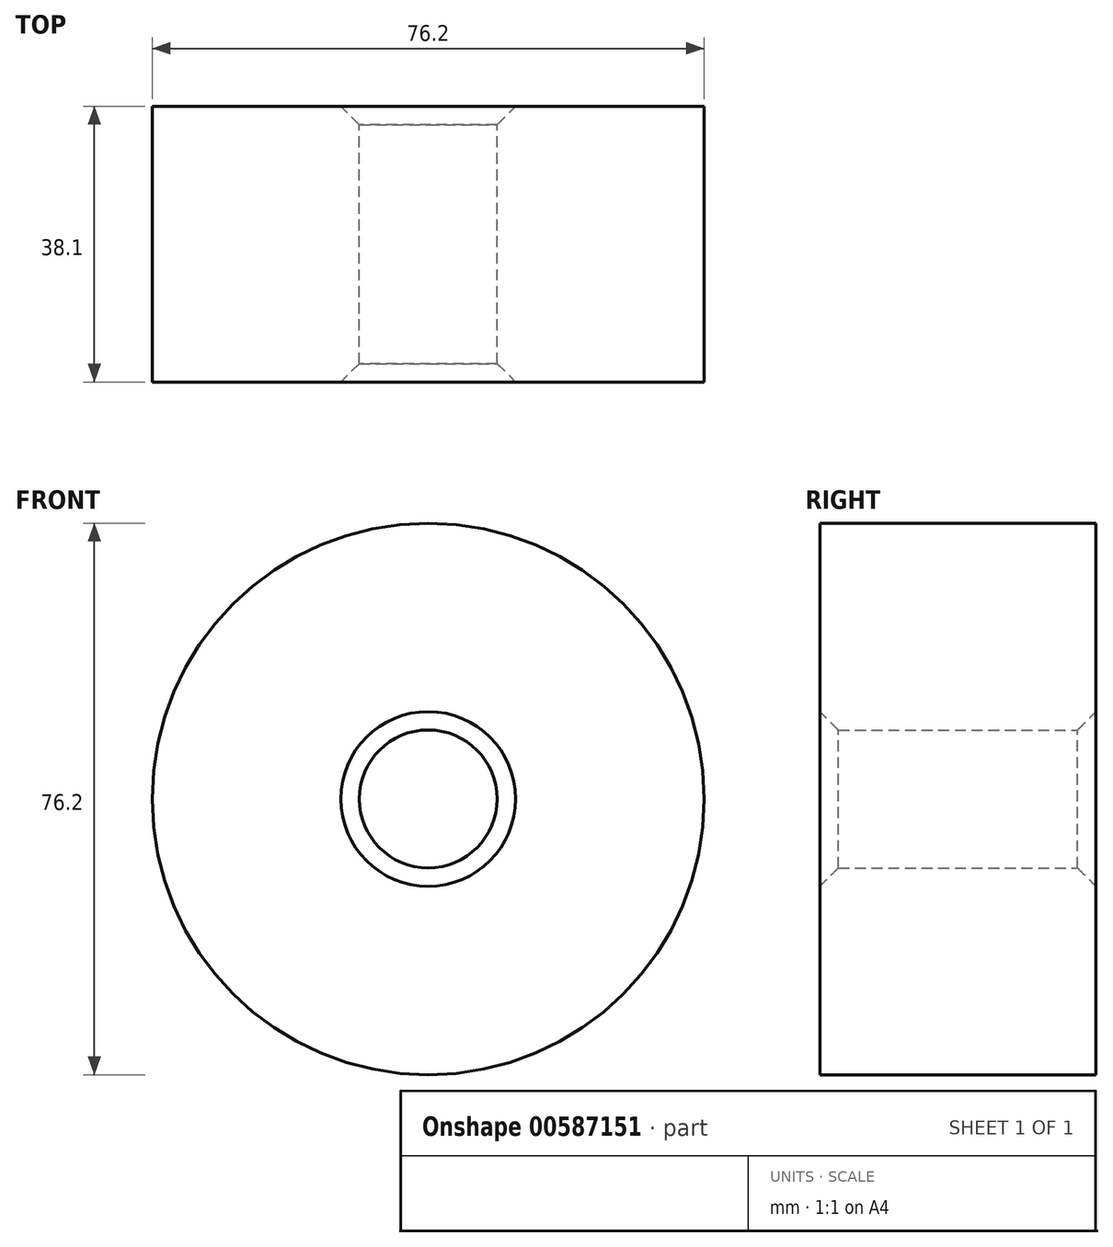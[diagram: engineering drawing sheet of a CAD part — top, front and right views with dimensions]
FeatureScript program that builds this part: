
annotation { "Feature Type Name" : "Feature", "Feature Type Description" : "" }
export const myFeature = defineFeature(function(context is Context, id is Id, definition is map)
    precondition{}
    {
        {
            var Q0;
            Q0=qCreatedBy(makeId("Front.planeOp"),FACE);
            var sketch = newSketch(context, id + "F0", { "sketchPlane" : qUnion([Q0])});
            skCircle(sketch, "E0", {"center": v(-51.5, 0) * mm, "radius": 38.1 * mm});
            skCircle(sketch, "E1", {"center": v(75.5, 0) * mm, "radius": 25.4 * mm});
            skCircle(sketch, "E2", {"center": v(-51.5, 0) * mm, "radius": 9.53 * mm});
            skCircle(sketch, "E3", {"center": v(75.5, 0) * mm, "radius": 9.53 * mm});
            skSolve(sketch);
        }
        {
            var Q0;
            Q0 = qSketchRegion(id + "F0", true);
            var sketch = newSketch(context, id + "F1", { "sketchPlane" : qUnion([Q0])});
            skLineSegment(sketch, "E4", {"start": v(-50.16, 38.16) * mm, "end": v(78.48, 25.23) * mm});
            skLineSegment(sketch, "E5", {"start": v(-53.26, -38.47) * mm, "end": v(78.52, -25.22) * mm});
            skSolve(sketch);
        }
        {
            var Q0;
            Q0=makeQuery(id+"F1.imprint","IMPRINT",FACE,{"disambiguationData":[TD([[makeQuery(id+"F1.imprint","IMPRINT",EDGE,{"derivedFrom":makeQuery(id+"F0.imprint","IMPRINT",EDGE,{"derivedFrom":sQuery(id+"F0.wireOp",EDGE,"E2")})}),-1.0]])]});
            var Q1;
            {var subQ0=sQuery(id+"F1.wireOp",EDGE,"E4");var subQ1=makeQuery(id+"F0.imprint","IMPRINT",EDGE,{"derivedFrom":sQuery(id+"F0.wireOp",EDGE,"E0")});var subQ2=makeQuery(id+"F1.imprint","INTERSECT",VERTEX,{"derivedFrom":[subQ1,subQ0]});Q1=makeQuery(id+"F1.imprint","IMPRINT",FACE,{"disambiguationData":[TD([[makeQuery(id+"F1.imprint","IMPRINT",EDGE,{"disambiguationData":[TD([[subQ2,-1.0]])],"derivedFrom":subQ0}),-1.0]])]});}
            var Q2;
            Q2=makeQuery(id+"F1.imprint","IMPRINT",FACE,{"disambiguationData":[TD([[makeQuery(id+"F1.imprint","IMPRINT",EDGE,{"derivedFrom":makeQuery(id+"F0.imprint","IMPRINT",EDGE,{"derivedFrom":sQuery(id+"F0.wireOp",EDGE,"E3")})}),-1.0]])]});
            extrude(context, id + "F2", {"entities" : qUnion([Q0, Q1, Q2]), "depth" : 25.4 * mm, "offsetDistance" : 25.4 * mm});
        }
        {
            var Q0;
            Q0=makeQuery(id+"F0.imprint","IMPRINT",FACE,{"disambiguationData":[TD([[makeQuery(id+"F0.imprint","IMPRINT",EDGE,{"derivedFrom":sQuery(id+"F0.wireOp",EDGE,"E0")}),1.0]])]});
            extrude(context, id + "F3", {"entities" : qUnion([Q0]), "operationType" : NewBodyOperationType.ADD, "depth" : 38.1 * mm, "offsetDistance" : 25.4 * mm});
        }
        {
            var Q0;
            Q0=makeQuery(id+"F2.opExtrude","SWEPT_FACE",FACE,{"disambiguationData":[OSD([sQuery(id+"F0.wireOp",EDGE,"E3")])]});
            var Q1;
            {var subQ0=sQuery(id+"F0.wireOp",EDGE,"E2");Q1=makeQuery(id+"F3.boolean.opBoolean","MERGE",FACE,{"derivedFrom":[makeQuery(id+"F2.opExtrude","SWEPT_FACE",FACE,{"disambiguationData":[OSD([subQ0])]}),makeQuery(id+"F3.opExtrude","SWEPT_FACE",FACE,{"disambiguationData":[OSD([subQ0])]})]});}
            chamfer(context, id + "F4", {"entities" : qUnion([Q0, Q1]), "width" : 2.54 * mm, "tangentPropagation" : true});
        }
    });
